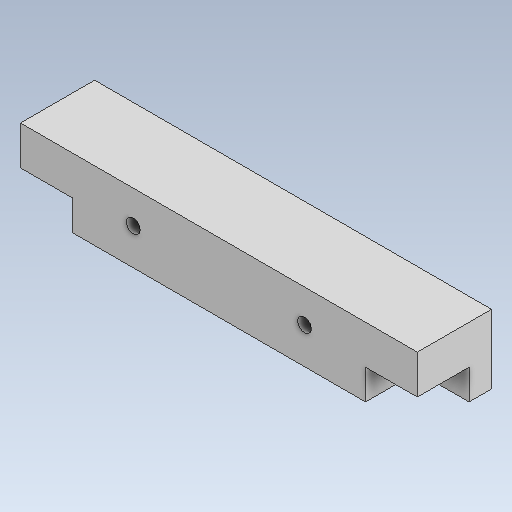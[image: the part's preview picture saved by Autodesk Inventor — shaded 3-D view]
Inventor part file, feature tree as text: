
AUTODESK INVENTOR PART (.ipt)
format: ipt  version: 2020 (Build 240168000, 168)  size: 128,000 bytes
history: native  units: mm
features: other x4, mirror x1
ambient origin geometry x8: Origin, YZ Plane, XZ Plane, XY Plane, X Axis, Y Axis, Z Axis, Center Point
bodies: Body1 (feature_tree)
feature tree (5):
  other  "side_bumper_upper_R.ipt"
  mirror  "미러1"
  other  "솔리드2::side_bumper_upper_R.ipt"
  other  "피쳐 태그1"
  other  "솔리드1"
